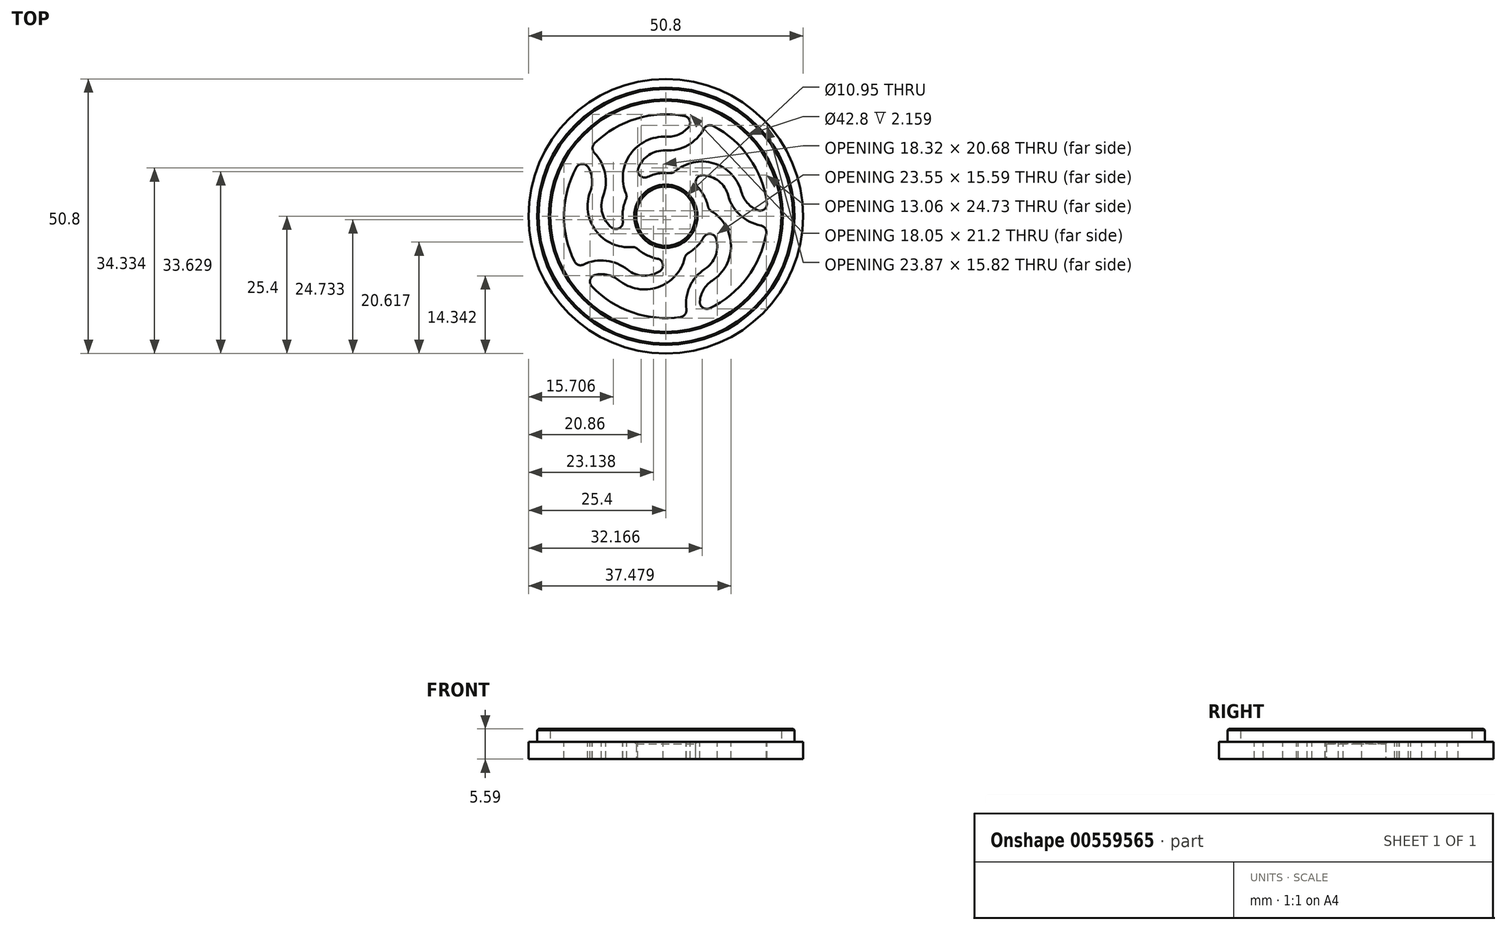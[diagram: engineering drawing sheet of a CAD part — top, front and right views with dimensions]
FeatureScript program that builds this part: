
annotation { "Feature Type Name" : "Feature", "Feature Type Description" : "" }
export const myFeature = defineFeature(function(context is Context, id is Id, definition is map)
    precondition{}
    {
        {
            var Q0;
            Q0=qCreatedBy(makeId("Front.planeOp"),FACE);
            var sketch = newSketch(context, id + "F0", { "sketchPlane" : qUnion([Q0])});
            skLineSegment(sketch, "E0", {"start": v(-5.47, 0) * mm, "end": v(-25.4, 0) * mm});
            skLineSegment(sketch, "E1", {"start": v(-25.4, 0) * mm, "end": v(-25.4, 3.17) * mm});
            skLineSegment(sketch, "E2", {"start": v(-25.4, 3.17) * mm, "end": v(-23.81, 3.17) * mm});
            skLineSegment(sketch, "E3", {"start": v(-23.81, 3.17) * mm, "end": v(-23.81, 5.33) * mm});
            skLineSegment(sketch, "E4", {"start": v(-23.56, 5.59) * mm, "end": v(-21.65, 5.59) * mm});
            skLineSegment(sketch, "E5", {"start": v(-21.4, 5.33) * mm, "end": v(-21.4, 3.17) * mm});
            skLineSegment(sketch, "E6", {"start": v(-21.4, 3.17) * mm, "end": v(-5.85, 3.17) * mm});
            skLineSegment(sketch, "E7", {"start": v(-5.47, 2.8) * mm, "end": v(-5.47, 0) * mm});
            skLineSegment(sketch, "E8", {"start": v(-5.85, 3.18) * mm, "end": v(-5.47, 2.8) * mm});
            skPoint(sketch, "E9.orphan", {"position": v(-5.47, 3.17) * mm});
            skLineSegment(sketch, "E10", {"start": v(-23.81, 5.33) * mm, "end": v(-23.56, 5.59) * mm});
            skLineSegment(sketch, "E11", {"start": v(-21.65, 5.59) * mm, "end": v(-21.4, 5.33) * mm});
            skLineSegment(sketch, "E12", {"start": v(0, 0) * mm, "end": v(0, 14.35) * mm, "construction": true});
            skSolve(sketch);
        }
        {
            var Q0;
            Q0=makeQuery(id+"F0.imprint","IMPRINT",FACE,{"disambiguationData":[TD([[makeQuery(id+"F0.imprint","IMPRINT",EDGE,{"derivedFrom":sQuery(id+"F0.wireOp",EDGE,"E0")}),-1.0]])]});
            var Q1;
            Q1=sQuery(id+"F0.wireOp",EDGE,"E12");
            revolve(context, id + "F1", {"entities" : qUnion([Q0]), "axis" : qUnion([Q1]), "revolveType" : RevolveType.FULL});
        }
        {
            var Q0;
            Q0=makeQuery(id+"F1.opRevolve","SWEPT_FACE",FACE,{"disambiguationData":[OSD([sQuery(id+"F0.wireOp",EDGE,"E6")])]});
            var sketch = newSketch(context, id + "F2", { "sketchPlane" : qUnion([Q0])});
            skArc(sketch, "E13", {"start": v(-7.36, 3.16) * mm, "mid": v(5.75, -5.59) * mm, "end": v(-3.37, 7.27) * mm});
            skArc(sketch, "E14", {"start": v(3.45, 18.54) * mm, "mid": v(-6.17, -17.82) * mm, "end": v(8.76, 16.7) * mm});
            skLineSegment(sketch, "E15", {"start": v(0, 18.86) * mm, "end": v(0, 8.01) * mm, "construction": true});
            skArc(sketch, "E16", {"start": v(0, 13.44) * mm, "mid": v(-5.43, 10.88) * mm, "end": v(-6.3, 4.95) * mm, "construction": true});
            skArc(sketch, "E17", {"start": v(0, 13.44) * mm, "mid": v(3.9, 14.53) * mm, "end": v(6.35, 17.76) * mm, "construction": true});
            skArc(sketch, "E18.0", {"start": v(-0.07, 12.17) * mm, "mid": v(4.07, 13.14) * mm, "end": v(7.05, 16.18) * mm});
            skArc(sketch, "E18.1", {"start": v(-0.07, 12.17) * mm, "mid": v(-3.12, 11.34) * mm, "end": v(-5.1, 8.87) * mm});
            skArc(sketch, "E19.0", {"start": v(0.07, 14.7) * mm, "mid": v(2.33, 15.1) * mm, "end": v(4.18, 16.46) * mm});
            skArc(sketch, "E19.1", {"start": v(0.07, 14.7) * mm, "mid": v(-6.56, 11.48) * mm, "end": v(-7.36, 4.15) * mm});
            skPoint(sketch, "E20.visualSharp", {"position": v(-7.13, 3.66) * mm});
            skArc(sketch, "E20.filletArc", {"start": v(-7.36, 3.16) * mm, "mid": v(-7.26, 3.66) * mm, "end": v(-7.36, 4.15) * mm});
            skPoint(sketch, "E21.visualSharp", {"position": v(-5.3, 6.02) * mm});
            skArc(sketch, "E21.filletArc", {"start": v(-5.1, 8.87) * mm, "mid": v(-4.76, 7.5) * mm, "end": v(-3.37, 7.27) * mm});
            skPoint(sketch, "E22.visualSharp", {"position": v(7.53, 17.3) * mm});
            skArc(sketch, "E22.filletArc", {"start": v(8.76, 16.7) * mm, "mid": v(7.8, 16.8) * mm, "end": v(7.05, 16.18) * mm});
            skPoint(sketch, "E23.visualSharp", {"position": v(5.14, 18.15) * mm});
            skArc(sketch, "E23.filletArc", {"start": v(4.18, 16.46) * mm, "mid": v(4.42, 17.71) * mm, "end": v(3.45, 18.54) * mm});
            skArc(sketch, "E24.1.0", {"start": v(-14.37, 9.06) * mm, "mid": v(-15.48, 9.67) * mm, "end": v(-16.57, 9.01) * mm});
            skArc(sketch, "E24.1.1", {"start": v(-13.96, 4.6) * mm, "mid": v(-13.65, 6.88) * mm, "end": v(-14.37, 9.06) * mm});
            skArc(sketch, "E24.1.2", {"start": v(-13.96, 4.6) * mm, "mid": v(-12.95, -2.7) * mm, "end": v(-6.22, -5.72) * mm});
            skArc(sketch, "E24.1.3", {"start": v(-5.28, -6.03) * mm, "mid": v(-5.72, -5.78) * mm, "end": v(-6.22, -5.72) * mm});
            skArc(sketch, "E24.1.4", {"start": v(-10, -2.1) * mm, "mid": v(-8.6, -2.21) * mm, "end": v(-7.96, -0.95) * mm});
            skArc(sketch, "E24.1.5", {"start": v(-11.6, 3.7) * mm, "mid": v(-11.75, 0.54) * mm, "end": v(-10, -2.1) * mm});
            skArc(sketch, "E24.1.6", {"start": v(-11.6, 3.7) * mm, "mid": v(-11.24, 7.93) * mm, "end": v(-13.2, 11.7) * mm});
            skArc(sketch, "E24.1.7", {"start": v(-13.18, 13.49) * mm, "mid": v(-13.56, 12.6) * mm, "end": v(-13.2, 11.7) * mm});
            skArc(sketch, "E24.2.0", {"start": v(-13.06, -10.86) * mm, "mid": v(-13.98, -11.74) * mm, "end": v(-13.69, -12.97) * mm});
            skArc(sketch, "E24.2.1", {"start": v(-8.7, -11.86) * mm, "mid": v(-10.76, -10.85) * mm, "end": v(-13.06, -10.86) * mm});
            skArc(sketch, "E24.2.2", {"start": v(-8.7, -11.86) * mm, "mid": v(-1.44, -13.14) * mm, "end": v(3.51, -7.69) * mm});
            skArc(sketch, "E24.2.3", {"start": v(4.1, -6.89) * mm, "mid": v(3.72, -7.23) * mm, "end": v(3.51, -7.69) * mm});
            skArc(sketch, "E24.2.4", {"start": v(-1.1, -10.17) * mm, "mid": v(-0.55, -8.86) * mm, "end": v(-1.55, -7.86) * mm});
            skArc(sketch, "E24.2.5", {"start": v(-7.1, -9.88) * mm, "mid": v(-4.14, -11) * mm, "end": v(-1.1, -10.17) * mm});
            skArc(sketch, "E24.2.6", {"start": v(-7.1, -9.88) * mm, "mid": v(-11.02, -8.24) * mm, "end": v(-15.21, -8.95) * mm});
            skArc(sketch, "E24.2.7", {"start": v(-16.9, -8.37) * mm, "mid": v(-16.18, -9) * mm, "end": v(-15.21, -8.95) * mm});
            skArc(sketch, "E24.3.0", {"start": v(6.3, -15.78) * mm, "mid": v(6.84, -16.93) * mm, "end": v(8.1, -17.03) * mm});
            skArc(sketch, "E24.3.1", {"start": v(8.59, -11.94) * mm, "mid": v(7, -13.59) * mm, "end": v(6.3, -15.78) * mm});
            skArc(sketch, "E24.3.2", {"start": v(8.59, -11.94) * mm, "mid": v(12.06, -5.43) * mm, "end": v(8.4, 0.97) * mm});
            skArc(sketch, "E24.3.3", {"start": v(7.82, 1.77) * mm, "mid": v(8.02, 1.3) * mm, "end": v(8.4, 0.97) * mm});
            skArc(sketch, "E24.3.4", {"start": v(9.33, -4.18) * mm, "mid": v(8.26, -3.26) * mm, "end": v(7, -3.9) * mm});
            skArc(sketch, "E24.3.5", {"start": v(7.2, -9.8) * mm, "mid": v(9.19, -7.34) * mm, "end": v(9.33, -4.18) * mm});
            skArc(sketch, "E24.3.6", {"start": v(7.2, -9.8) * mm, "mid": v(4.43, -13.02) * mm, "end": v(3.8, -17.23) * mm});
            skArc(sketch, "E24.3.7", {"start": v(2.74, -18.66) * mm, "mid": v(3.57, -18.17) * mm, "end": v(3.8, -17.23) * mm});
            skArc(sketch, "E24.4.0", {"start": v(16.95, 1.11) * mm, "mid": v(18.21, 1.27) * mm, "end": v(18.7, 2.45) * mm});
            skArc(sketch, "E24.4.1", {"start": v(14, 4.48) * mm, "mid": v(15.09, 2.46) * mm, "end": v(16.95, 1.11) * mm});
            skArc(sketch, "E24.4.2", {"start": v(14, 4.48) * mm, "mid": v(8.9, 9.79) * mm, "end": v(1.68, 8.28) * mm});
            skArc(sketch, "E24.4.3", {"start": v(0.73, 7.98) * mm, "mid": v(1.23, 8.04) * mm, "end": v(1.68, 8.28) * mm});
            skArc(sketch, "E24.4.4", {"start": v(6.86, 7.58) * mm, "mid": v(5.65, 6.85) * mm, "end": v(5.88, 5.45) * mm});
            skArc(sketch, "E24.4.5", {"start": v(11.55, 3.82) * mm, "mid": v(9.82, 6.47) * mm, "end": v(6.86, 7.58) * mm});
            skArc(sketch, "E24.4.6", {"start": v(11.55, 3.82) * mm, "mid": v(13.76, 0.19) * mm, "end": v(17.56, -1.7) * mm});
            skArc(sketch, "E24.4.7", {"start": v(18.6, -3.16) * mm, "mid": v(18.38, -2.22) * mm, "end": v(17.56, -1.7) * mm});
            skSolve(sketch);
        }
        {
            var Q0;
            Q0=makeQuery(id+"F2.imprint","IMPRINT",FACE,{"disambiguationData":[TD([[makeQuery(id+"F2.imprint","IMPRINT",EDGE,{"derivedFrom":sQuery(id+"F2.wireOp",EDGE,"E19.0")}),1.0]])]});
            var Q1;
            {var subQ0=sQuery(id+"F2.wireOp",EDGE,"E24.1.0");Q1=makeQuery(id+"F2.imprint","IMPRINT",FACE,{"disambiguationData":[TD([[makeQuery(id+"F2.imprint","IMPRINT",EDGE,{"derivedFrom":subQ0}),1.0]])]});}
            var Q2;
            Q2=makeQuery(id+"F2.imprint","IMPRINT",FACE,{"disambiguationData":[TD([[makeQuery(id+"F2.imprint","IMPRINT",EDGE,{"derivedFrom":sQuery(id+"F2.wireOp",EDGE,"E18.0")}),-1.0]])]});
            var Q3;
            {var subQ1=sQuery(id+"F2.wireOp",EDGE,"E24.3.0");Q3=makeQuery(id+"F2.imprint","IMPRINT",FACE,{"disambiguationData":[TD([[makeQuery(id+"F2.imprint","IMPRINT",EDGE,{"derivedFrom":subQ1}),1.0]])]});}
            var Q4;
            {var subQ0=sQuery(id+"F2.wireOp",EDGE,"E24.2.0");Q4=makeQuery(id+"F2.imprint","IMPRINT",FACE,{"disambiguationData":[TD([[makeQuery(id+"F2.imprint","IMPRINT",EDGE,{"derivedFrom":subQ0}),1.0]])]});}
            extrude(context, id + "F3", {"entities" : qUnion([Q0, Q1, Q2, Q3, Q4]), "operationType" : NewBodyOperationType.REMOVE, "oppositeDirection" : true, "depth" : 25.4 * mm, "offsetDistance" : 25.4 * mm});
        }
    });
